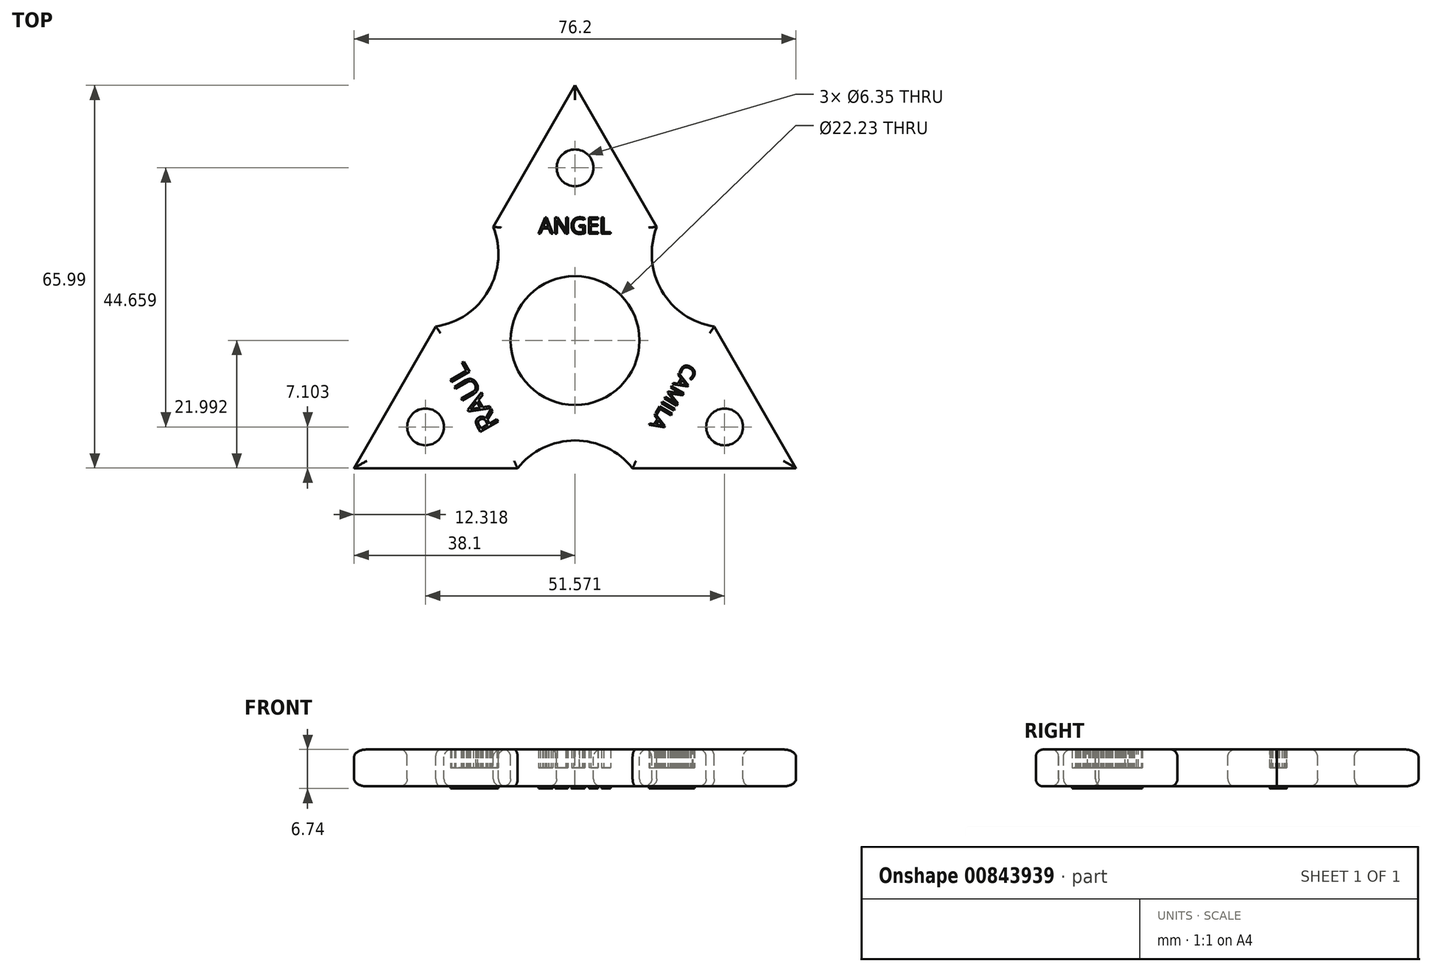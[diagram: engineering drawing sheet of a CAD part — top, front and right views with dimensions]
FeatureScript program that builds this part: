
annotation { "Feature Type Name" : "Feature", "Feature Type Description" : "" }
export const myFeature = defineFeature(function(context is Context, id is Id, definition is map)
    precondition{}
    {
        {
            var Q0;
            Q0=qCreatedBy(makeId("Top.planeOp"),FACE);
            var sketch = newSketch(context, id + "F0", { "sketchPlane" : qUnion([Q0])});
            skLineSegment(sketch, "E0", {"start": v(0, -24.21) * mm, "end": v(38.1, -24.21) * mm});
            skLineSegment(sketch, "E1", {"start": v(-38.1, -24.21) * mm, "end": v(0, -24.21) * mm});
            skLineSegment(sketch, "E2", {"start": v(38.1, -24.21) * mm, "end": v(0, 41.78) * mm});
            skLineSegment(sketch, "E3", {"start": v(0, 41.78) * mm, "end": v(-38.1, -24.21) * mm});
            skCircle(sketch, "E4", {"center": v(0, -2.22) * mm, "radius": 11.11 * mm});
            skCircle(sketch, "E5", {"center": v(25.92, 12.75) * mm, "radius": 12.7 * mm});
            skCircle(sketch, "E6", {"center": v(-25.92, 12.75) * mm, "radius": 12.7 * mm});
            skCircle(sketch, "E7", {"center": v(0, -32.15) * mm, "radius": 12.7 * mm});
            skCircle(sketch, "E8", {"center": v(25.79, -17.1) * mm, "radius": 3.18 * mm});
            skCircle(sketch, "E9", {"center": v(-25.78, -17.1) * mm, "radius": 3.18 * mm});
            skLineSegment(sketch, "E10", {"start": v(0, 41.78) * mm, "end": v(0, -24.21) * mm});
            skCircle(sketch, "E11", {"center": v(0, 27.55) * mm, "radius": 3.18 * mm});
            skSolve(sketch);
        }
        {
            var Q0;
            Q0=makeQuery(id+"F0.imprint","IMPRINT",FACE,{"disambiguationData":[TD([[makeQuery(id+"F0.imprint","IMPRINT",EDGE,{"derivedFrom":sQuery(id+"F0.wireOp",EDGE,"E9")}),-1.0]])]});
            var Q1;
            Q1=makeQuery(id+"F0.imprint","IMPRINT",FACE,{"disambiguationData":[TD([[makeQuery(id+"F0.imprint","IMPRINT",EDGE,{"derivedFrom":sQuery(id+"F0.wireOp",EDGE,"E8")}),-1.0]])]});
            extrude(context, id + "F1", {"entities" : qUnion([Q0, Q1]), "oppositeDirection" : true, "depth" : 3.17 * mm, "offsetDistance" : 25.4 * mm, "hasSecondDirection" : true, "secondDirectionOppositeDirection" : false, "secondDirectionDepth" : 3.17 * mm});
        }
        {
            var Q0;
            Q0=makeQuery(id+"F1.opExtrude","CAP_FACE",FACE,{"disambiguationData":[OSD([sQuery(id+"F0.wireOp",EDGE,"E0"),sQuery(id+"F0.wireOp",EDGE,"E1"),sQuery(id+"F0.wireOp",EDGE,"E2"),sQuery(id+"F0.wireOp",EDGE,"E3"),sQuery(id+"F0.wireOp",EDGE,"E4"),sQuery(id+"F0.wireOp",EDGE,"E5"),sQuery(id+"F0.wireOp",EDGE,"E6"),sQuery(id+"F0.wireOp",EDGE,"E7"),sQuery(id+"F0.wireOp",EDGE,"E8"),sQuery(id+"F0.wireOp",EDGE,"E9"),sQuery(id+"F0.wireOp",EDGE,"E11")])],"isStart":true});
            fillet(context, id + "F2", {"entities" : qUnion([Q0]), "radius" : 1.27 * mm, "tangentPropagation" : true, "allowEdgeOverflow" : false});
        }
        {
            var Q0;
            Q0=makeQuery(id+"F1.opExtrude","CAP_FACE",FACE,{"disambiguationData":[OSD([sQuery(id+"F0.wireOp",EDGE,"E0"),sQuery(id+"F0.wireOp",EDGE,"E1"),sQuery(id+"F0.wireOp",EDGE,"E2"),sQuery(id+"F0.wireOp",EDGE,"E3"),sQuery(id+"F0.wireOp",EDGE,"E4"),sQuery(id+"F0.wireOp",EDGE,"E5"),sQuery(id+"F0.wireOp",EDGE,"E6"),sQuery(id+"F0.wireOp",EDGE,"E7"),sQuery(id+"F0.wireOp",EDGE,"E8"),sQuery(id+"F0.wireOp",EDGE,"E9"),sQuery(id+"F0.wireOp",EDGE,"E11")])],"isStart":false});
            fillet(context, id + "F3", {"entities" : qUnion([Q0]), "radius" : 1.27 * mm, "tangentPropagation" : true, "allowEdgeOverflow" : false});
        }
        {
            var Q0;
            Q0=qCreatedBy(makeId("Top.planeOp"),FACE);
            var sketch = newSketch(context, id + "F4", { "sketchPlane" : qUnion([Q0])});
            skText(sketch, "E12", { "text": "ANGEL\n", "fontName": "OpenSans-Regular.ttf"});
            const initialGuessF4  = {"E12": [-0.0063, 0.01619, 1, 0, 0.00283]};
            skSetInitialGuess(sketch, initialGuessF4);
            skSolve(sketch);
        }
        {
            var Q0;
            Q0=qCreatedBy(makeId("Top.planeOp"),FACE);
            var sketch = newSketch(context, id + "F5", { "sketchPlane" : qUnion([Q0])});
            skText(sketch, "E13", { "text": "RAUL", "fontName": "OpenSans-Regular.ttf"});
            const initialGuessF5  = {"E13": [-0.013, -0.01658, -0.5, 0.86603, 0.0036]};
            skSetInitialGuess(sketch, initialGuessF5);
            skSolve(sketch);
        }
        {
            var Q0;
            Q0 = qSketchRegion(id + "F4", true);
            extrude(context, id + "F6", {"entities" : qUnion([Q0]), "operationType" : NewBodyOperationType.ADD, "oppositeDirection" : true, "depth" : 3.56 * mm, "offsetDistance" : 25.4 * mm, "hasSecondDirection" : true, "secondDirectionOppositeDirection" : false, "secondDirectionDepth" : 3.56 * mm});
        }
        {
            var Q0;
            Q0 = qSketchRegion(id + "F5", true);
            extrude(context, id + "F7", {"entities" : qUnion([Q0]), "operationType" : NewBodyOperationType.ADD, "oppositeDirection" : true, "depth" : 3.56 * mm, "offsetDistance" : 25.4 * mm, "hasSecondDirection" : true, "secondDirectionOppositeDirection" : false, "secondDirectionDepth" : 3.56 * mm});
        }
        {
            var Q0;
            Q0 = qSketchRegion(id + "F4", true);
            extrude(context, id + "F8", {"entities" : qUnion([Q0]), "operationType" : NewBodyOperationType.REMOVE, "depth" : 3.56 * mm, "offsetDistance" : 25.4 * mm});
        }
        {
            var Q0;
            Q0 = qSketchRegion(id + "F5", true);
            extrude(context, id + "F9", {"entities" : qUnion([Q0]), "operationType" : NewBodyOperationType.REMOVE, "depth" : 3.56 * mm, "offsetDistance" : 25.4 * mm});
        }
        {
            var Q0;
            Q0=qCreatedBy(makeId("Top.planeOp"),FACE);
            var sketch = newSketch(context, id + "F10", { "sketchPlane" : qUnion([Q0])});
            skText(sketch, "E14", { "text": "CAMILA", "fontName": "OpenSans-Regular.ttf"});
            const initialGuessF10  = {"E14": [0.01898, -0.00596, -0.5, -0.86603, 0.0025]};
            skSetInitialGuess(sketch, initialGuessF10);
            skSolve(sketch);
        }
        {
            var Q0;
            Q0 = qSketchRegion(id + "F10", true);
            extrude(context, id + "F11", {"entities" : qUnion([Q0]), "operationType" : NewBodyOperationType.ADD, "depth" : 3.56 * mm, "offsetDistance" : 25.4 * mm, "hasSecondDirection" : true, "secondDirectionOppositeDirection" : true, "secondDirectionDepth" : 3.56 * mm});
        }
        {
            var Q0;
            Q0 = qSketchRegion(id + "F10", true);
            extrude(context, id + "F12", {"entities" : qUnion([Q0]), "operationType" : NewBodyOperationType.REMOVE, "flatOperationType" : FlatOperationType.REMOVE, "depth" : 3.56 * mm, "offsetDistance" : 25.4 * mm, "domain" : OperationDomain.MODEL});
        }
    });
